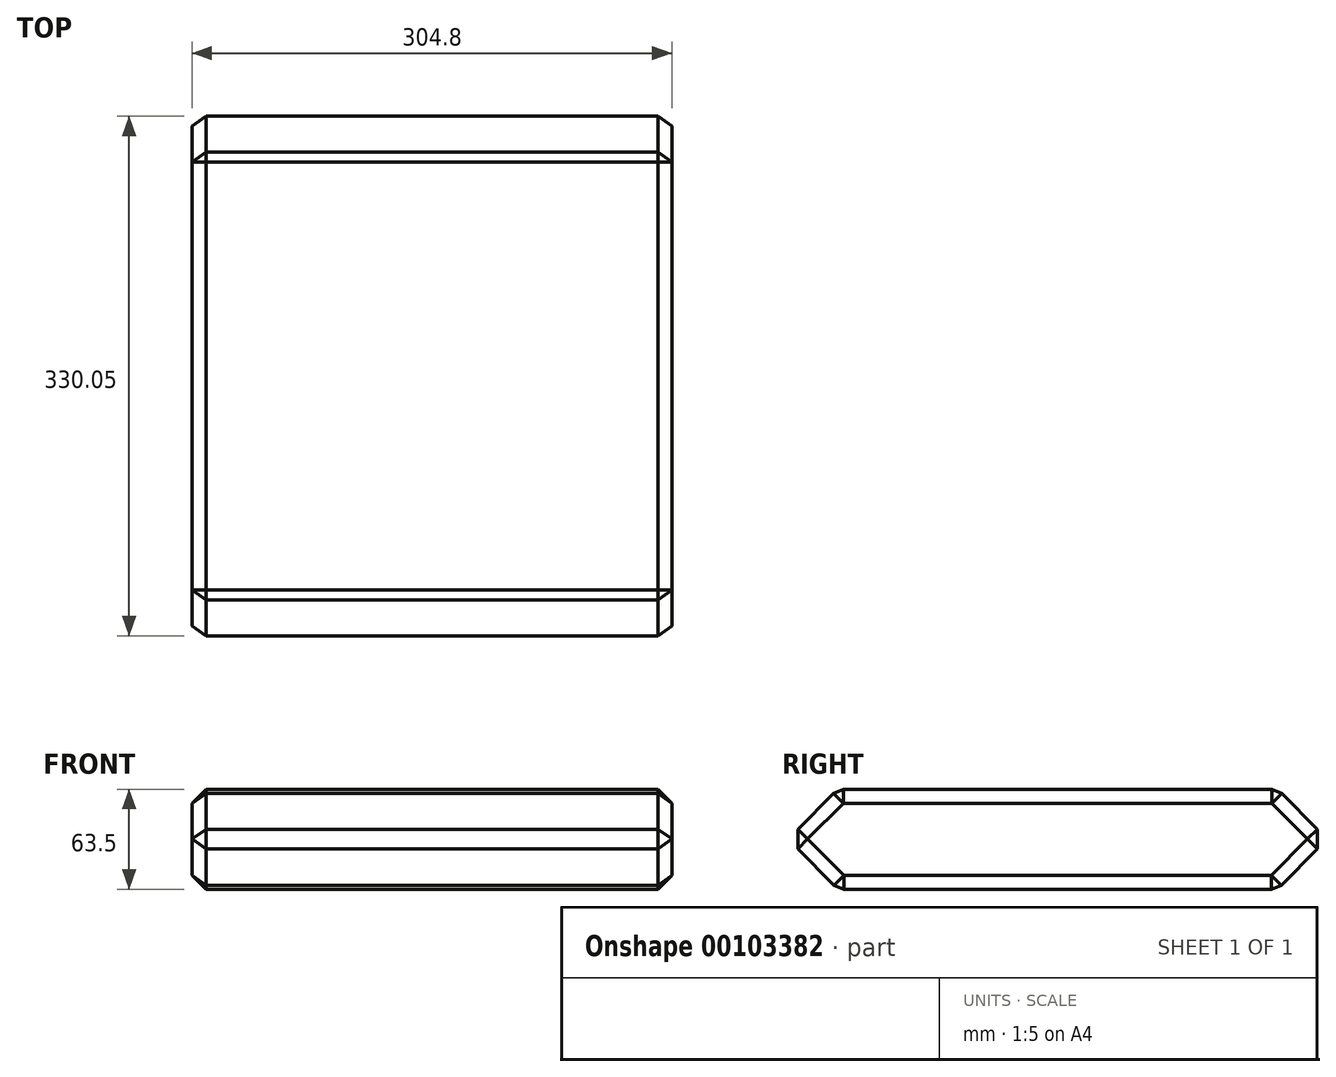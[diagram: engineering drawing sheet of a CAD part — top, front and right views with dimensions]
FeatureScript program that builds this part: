
annotation { "Feature Type Name" : "Feature", "Feature Type Description" : "" }
export const myFeature = defineFeature(function(context is Context, id is Id, definition is map)
    precondition{}
    {
        {
            var Q0;
            Q0=qCreatedBy(makeId("Right.planeOp"),FACE);
            var sketch = newSketch(context, id + "F0", { "sketchPlane" : qUnion([Q0])});
            skLineSegment(sketch, "E0", {"start": v(-11.89, 31.61) * mm, "end": v(-43.5, 0) * mm});
            skLineSegment(sketch, "E1", {"start": v(-43.5, 0) * mm, "end": v(-11.6, -31.89) * mm});
            skLineSegment(sketch, "E2", {"start": v(-11.6, -31.89) * mm, "end": v(267.23, -31.89) * mm});
            skLineSegment(sketch, "E3", {"start": v(267.23, -31.89) * mm, "end": v(299.12, 0) * mm});
            skLineSegment(sketch, "E4", {"start": v(299.12, 0) * mm, "end": v(267.51, 31.61) * mm});
            skLineSegment(sketch, "E5", {"start": v(267.51, 31.61) * mm, "end": v(-11.89, 31.61) * mm});
            skSolve(sketch);
        }
        {
            var Q0;
            Q0=makeQuery(id+"F0.imprint","IMPRINT",FACE,{"disambiguationData":[TD([[makeQuery(id+"F0.imprint","IMPRINT",EDGE,{"derivedFrom":sQuery(id+"F0.wireOp",EDGE,"E0")}),1.0]])]});
            extrude(context, id + "F1", {"entities" : qUnion([Q0]), "depth" : 304.8 * mm});
        }
        {
            var Q0;
            Q0=makeQuery(id+"F1.opExtrude","SWEPT_FACE",FACE,{"disambiguationData":[OSD([sQuery(id+"F0.wireOp",EDGE,"E4")])]});
            var Q1;
            Q1=makeQuery(id+"F1.opExtrude","SWEPT_FACE",FACE,{"disambiguationData":[OSD([sQuery(id+"F0.wireOp",EDGE,"E5")])]});
            var Q2;
            Q2=makeQuery(id+"F1.opExtrude","CAP_FACE",FACE,{"disambiguationData":[OSD([sQuery(id+"F0.wireOp",EDGE,"E0"),sQuery(id+"F0.wireOp",EDGE,"E1"),sQuery(id+"F0.wireOp",EDGE,"E2"),sQuery(id+"F0.wireOp",EDGE,"E3"),sQuery(id+"F0.wireOp",EDGE,"E4"),sQuery(id+"F0.wireOp",EDGE,"E5")])],"isStart":false});
            var Q3;
            Q3=makeQuery(id+"F1.opExtrude","SWEPT_FACE",FACE,{"disambiguationData":[OSD([sQuery(id+"F0.wireOp",EDGE,"E3")])]});
            var Q4;
            Q4=makeQuery(id+"F1.opExtrude","SWEPT_FACE",FACE,{"disambiguationData":[OSD([sQuery(id+"F0.wireOp",EDGE,"E2")])]});
            var Q5;
            Q5=makeQuery(id+"F1.opExtrude","CAP_FACE",FACE,{"disambiguationData":[OSD([sQuery(id+"F0.wireOp",EDGE,"E0"),sQuery(id+"F0.wireOp",EDGE,"E1"),sQuery(id+"F0.wireOp",EDGE,"E2"),sQuery(id+"F0.wireOp",EDGE,"E3"),sQuery(id+"F0.wireOp",EDGE,"E4"),sQuery(id+"F0.wireOp",EDGE,"E5")])],"isStart":true});
            var Q6;
            Q6=makeQuery(id+"F1.opExtrude","SWEPT_FACE",FACE,{"disambiguationData":[OSD([sQuery(id+"F0.wireOp",EDGE,"E0")])]});
            var Q7;
            Q7=makeQuery(id+"F1.opExtrude","SWEPT_FACE",FACE,{"disambiguationData":[OSD([sQuery(id+"F0.wireOp",EDGE,"E1")])]});
            chamfer(context, id + "F2", {"entities" : qUnion([Q0, Q1, Q2, Q3, Q4, Q5, Q6, Q7]), "width" : 8.9 * mm, "tangentPropagation" : true});
        }
    });
